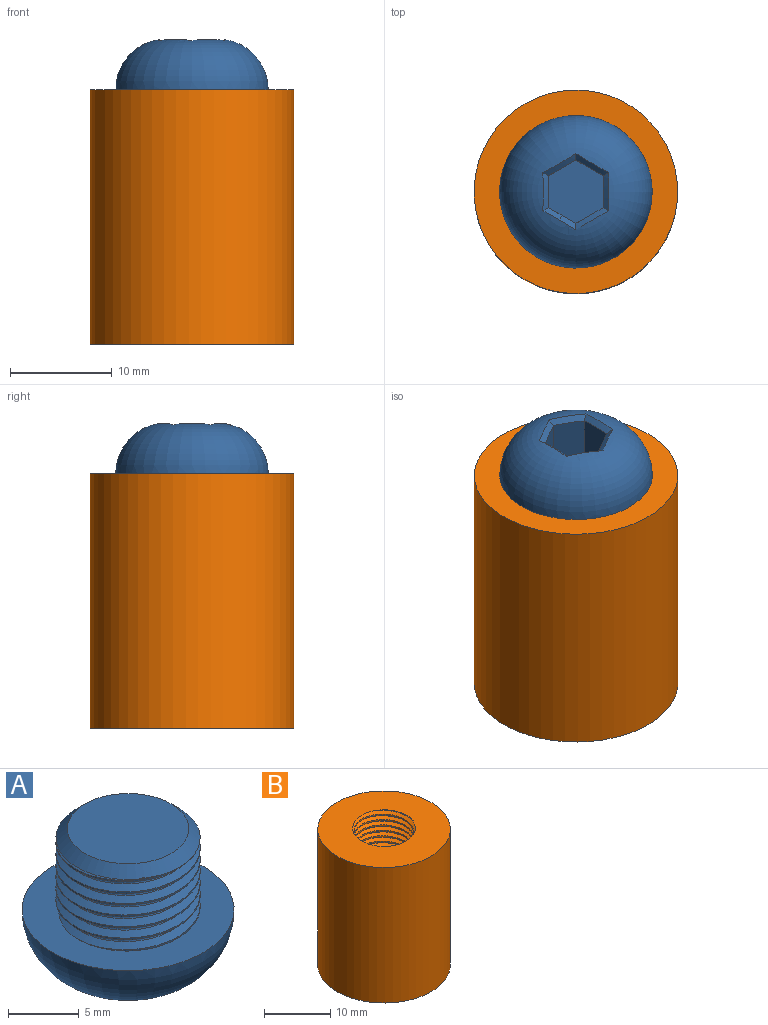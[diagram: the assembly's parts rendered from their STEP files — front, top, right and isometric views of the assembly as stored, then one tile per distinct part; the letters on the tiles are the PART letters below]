
ASSEMBLY  parts=2 mates=1
PART A: 23 faces, bbox 15.3x15.3x12.2 mm
  f0: plane 7.62x2.81mm, normal (-0.5,0.87,0), area 23.3mm2, adj f1,f5,f10,f21
  f1: plane 7.62x2.81mm, normal (0.5,0.87,0), area 23.3mm2, adj f0,f2,f10,f19
  f2: plane 7.62x3.23mm, normal (1,0,0), area 23.3mm2, adj f1,f3,f10,f17
  f3: plane 7.62x2.81mm, normal (0.5,-0.87,0), area 23.3mm2, adj f2,f4,f10,f16
  f4: plane 7.62x2.81mm, normal (-0.5,-0.87,0), area 23.3mm2, adj f3,f5,f10,f18
  f5: plane 7.63x3.24mm, normal (-1,0,0), area 23.3mm2, adj f0,f4,f10,f20,f22
  f6: cylinder r=5.1mm len=10.2mm, axis (0,0,-1), area 26mm2, adj f8,f11,f13,f14
  f7: plane 8.6x8.6mm, normal (0,0,1), area 58.1mm2, adj f11
  f8: plane 15.28x15.28mm, normal (0,0,1), area 104.6mm2, adj f6,f9,f12,f13,f14
  f9: torus R=2.5mm, axis (0,0,1), area 263.6mm2, adj f8,f16,f17,f18,f19,f20,f21,f22
  f10: plane 6.24x5.4mm, normal (0,0,-1), area 25.3mm2, adj f0,f1,f2,f3,f4,f5
  f11: cone r=4.3mm half-angle=45deg, axis (0,0,-1), area 33.4mm2, adj f6,f7,f15
  f12: bspline ~10.53x9.12mm, area 49.3mm2, adj f8,f13,f14,f15
  f13: bspline ~11.78x10.2mm, area 117.8mm2, adj f6,f8,f12,f15
  f14: bspline ~11.78x10.2mm, area 117.6mm2, adj f6,f8,f12,f15
  f15: plane 10.47x10.23mm, normal (0,0,-1), area 9.6mm2, adj f11,f12,f13,f14
  f16: bspline ~3.47x2.32mm, area 2.4mm2, adj f3,f9,f17,f18
  f17: bspline ~3.75x0.55mm, area 2.4mm2, adj f2,f9,f16,f19
  f18: bspline ~3.47x2.32mm, area 2.4mm2, adj f4,f9,f16,f20
  f19: bspline ~3.47x2.32mm, area 2.4mm2, adj f1,f9,f17,f21
  f20: bspline ~1.87x0.55mm, area 1.2mm2, adj f5,f9,f18,f22
  f21: bspline ~3.47x2.32mm, area 2.4mm2, adj f0,f9,f19,f22
  f22: bspline ~1.97x0.55mm, area 1.2mm2, adj f5,f9,f20,f21
PART B: 7 faces, bbox 20.3x20.3x26.1 mm
  f0: cylinder r=10mm len=25mm, axis (0,0,-1), area 1570.8mm2, adj f1,f2
  f1: plane 20.3x20.3mm, normal (0,0,1), area 243.5mm2, adj f0,f3,f4,f5,f6
  f2: plane 20.3x20.3mm, normal (0,0,-1), area 243.5mm2, adj f0,f3,f4,f5,f6
  f3: bspline ~25.65x11.64mm, area 467.3mm2, adj f1,f2,f5,f6
  f4: bspline ~25.81x11.64mm, area 469.7mm2, adj f1,f2,f5,f6
  f5: bspline ~25.46x11.75mm, area 115mm2, adj f1,f2,f3,f4
  f6: cylinder r=4.5mm len=25mm, axis (0,0,1), area 309.5mm2, adj f1,f2,f3,f4
PLACE A rot(axis=(0.5,-0.87,0),180deg) t=(-53.06,-38.47,14.23)mm
PLACE B t=(27.31,52.52,-15.77)mm
MATE cylindrical A.f6 <-> B.f0  axis (0,0,-1) through (-4.61,-0.63,9.23)mm
